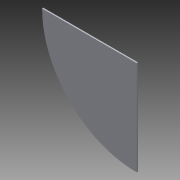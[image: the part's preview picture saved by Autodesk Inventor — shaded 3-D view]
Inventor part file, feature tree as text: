
AUTODESK INVENTOR PART (.ipt)
format: ipt  version: 2015 (Build 190159000, 159)  size: 76,800 bytes
history: native  units: mm
features: extrude x1, sketch x1
ambient origin geometry x8: Origin, YZ Plane, XZ Plane, XY Plane, X Axis, Y Axis, Z Axis, Center Point
bodies: Solid1 (feature_tree)
feature tree (2):
  extrude  "Extrusion1"  TaperAngle=90.0deg  [1 undecoded]
  sketch  "Sketch1"  dims[d0=300.0mm d1=90.0deg d2=4.0mm d3=0.0mm]
note: 1 required parameter value undecoded (feature->parameter linkage not recoverable at this tier; creation-order binding heuristic only, values carry confidence <= 0.55)
